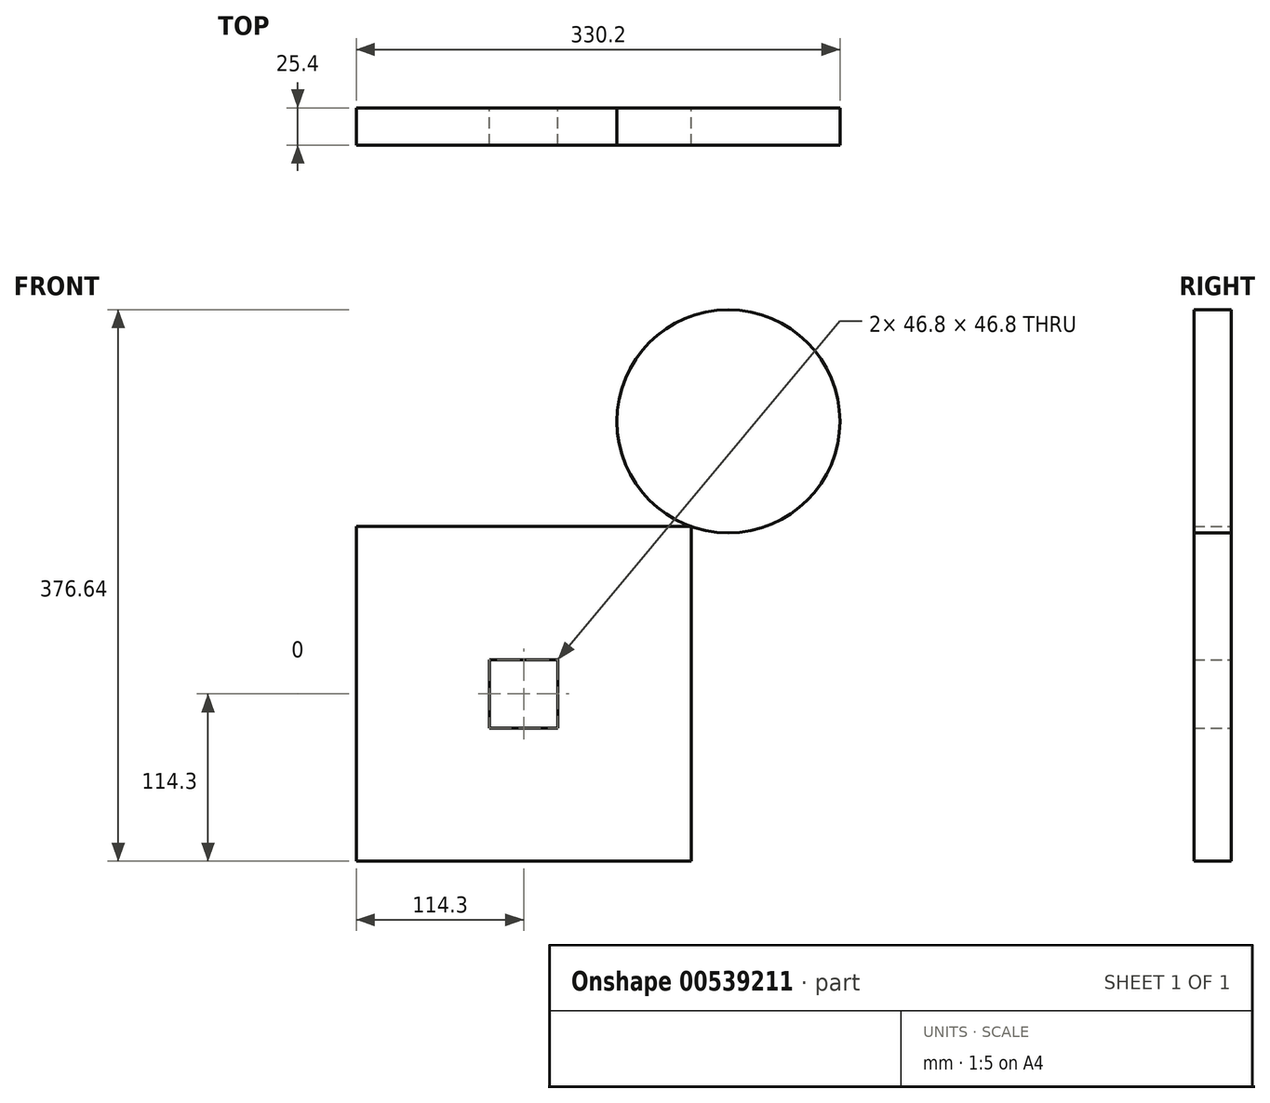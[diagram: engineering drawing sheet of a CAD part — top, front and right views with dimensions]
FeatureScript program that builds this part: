
annotation { "Feature Type Name" : "Feature", "Feature Type Description" : "" }
export const myFeature = defineFeature(function(context is Context, id is Id, definition is map)
    precondition{}
    {
        {
            var Q0;
            Q0=qCreatedBy(makeId("Front.planeOp"),FACE);
            var sketch = newSketch(context, id + "F0", { "sketchPlane" : qUnion([Q0])});
            skLineSegment(sketch, "E0", {"start": v(-25.4, 254) * mm, "end": v(-254, 254) * mm});
            skLineSegment(sketch, "E1", {"start": v(-254, 254) * mm, "end": v(-254, 25.4) * mm});
            skLineSegment(sketch, "E2", {"start": v(-254, 25.4) * mm, "end": v(-25.4, 25.4) * mm});
            skLineSegment(sketch, "E3", {"start": v(-25.4, 25.4) * mm, "end": v(-25.4, 254) * mm});
            skCircle(sketch, "E4", {"center": v(0, 325.84) * mm, "radius": 76.2 * mm});
            skLineSegment(sketch, "E5", {"start": v(-254, 254) * mm, "end": v(-25.4, 25.4) * mm, "construction": true});
            skLineSegment(sketch, "E6.bottom", {"start": v(-116.3, 163.1) * mm, "end": v(-163.1, 163.1) * mm});
            skLineSegment(sketch, "E6.top", {"start": v(-116.3, 116.3) * mm, "end": v(-163.1, 116.3) * mm});
            skLineSegment(sketch, "E6.left", {"start": v(-116.3, 163.1) * mm, "end": v(-116.3, 116.3) * mm});
            skLineSegment(sketch, "E6.right", {"start": v(-163.1, 163.1) * mm, "end": v(-163.1, 116.3) * mm});
            skPoint(sketch, "E6.middle", {"position": v(-139.7, 139.7) * mm});
            skSolve(sketch);
        }
        {
            var Q0;
            Q0=makeQuery(id+"F0.imprint","IMPRINT",FACE,{"disambiguationData":[TD([[makeQuery(id+"F0.imprint","IMPRINT",EDGE,{"derivedFrom":sQuery(id+"F0.wireOp",EDGE,"E0")}),1.0]])]});
            var Q1;
            Q1=makeQuery(id+"F0.imprint","IMPRINT",FACE,{"disambiguationData":[TD([[makeQuery(id+"F0.imprint","IMPRINT",EDGE,{"derivedFrom":sQuery(id+"F0.wireOp",EDGE,"E4")}),1.0]])]});
            extrude(context, id + "F1", {"entities" : qUnion([Q0, Q1]), "depth" : 25.4 * mm, "offsetDistance" : 25.4 * mm});
        }
    });
